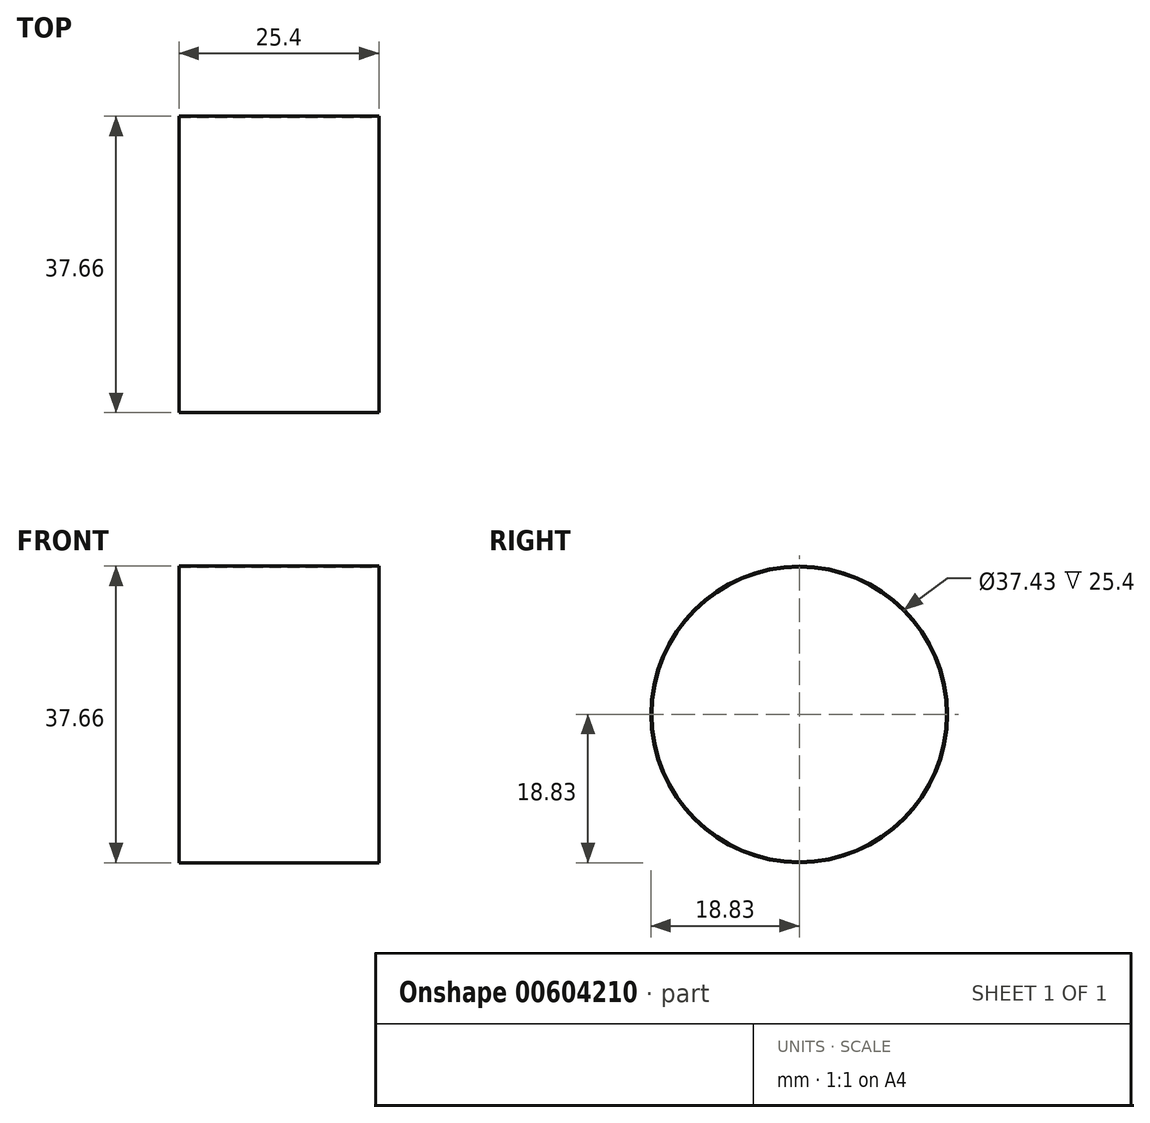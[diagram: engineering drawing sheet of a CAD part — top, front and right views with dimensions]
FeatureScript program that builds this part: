
annotation { "Feature Type Name" : "Feature", "Feature Type Description" : "" }
export const myFeature = defineFeature(function(context is Context, id is Id, definition is map)
    precondition{}
    {
        {
            var Q0;
            Q0=qCreatedBy(makeId("Right.planeOp"),FACE);
            var sketch = newSketch(context, id + "F0", { "sketchPlane" : qUnion([Q0])});
            skCircle(sketch, "E0", {"center": v(0, 0) * mm, "radius": 18.83 * mm});
            skCircle(sketch, "E1", {"center": v(0, 0) * mm, "radius": 18.71 * mm});
            skSolve(sketch);
        }
        {
            var Q0;
            Q0 = qSketchRegion(id + "F0", true);
            extrude(context, id + "F1", {"entities" : qUnion([Q0]), "oppositeDirection" : true, "depth" : 25.4 * mm, "offsetDistance" : 25.4 * mm});
        }
    });
